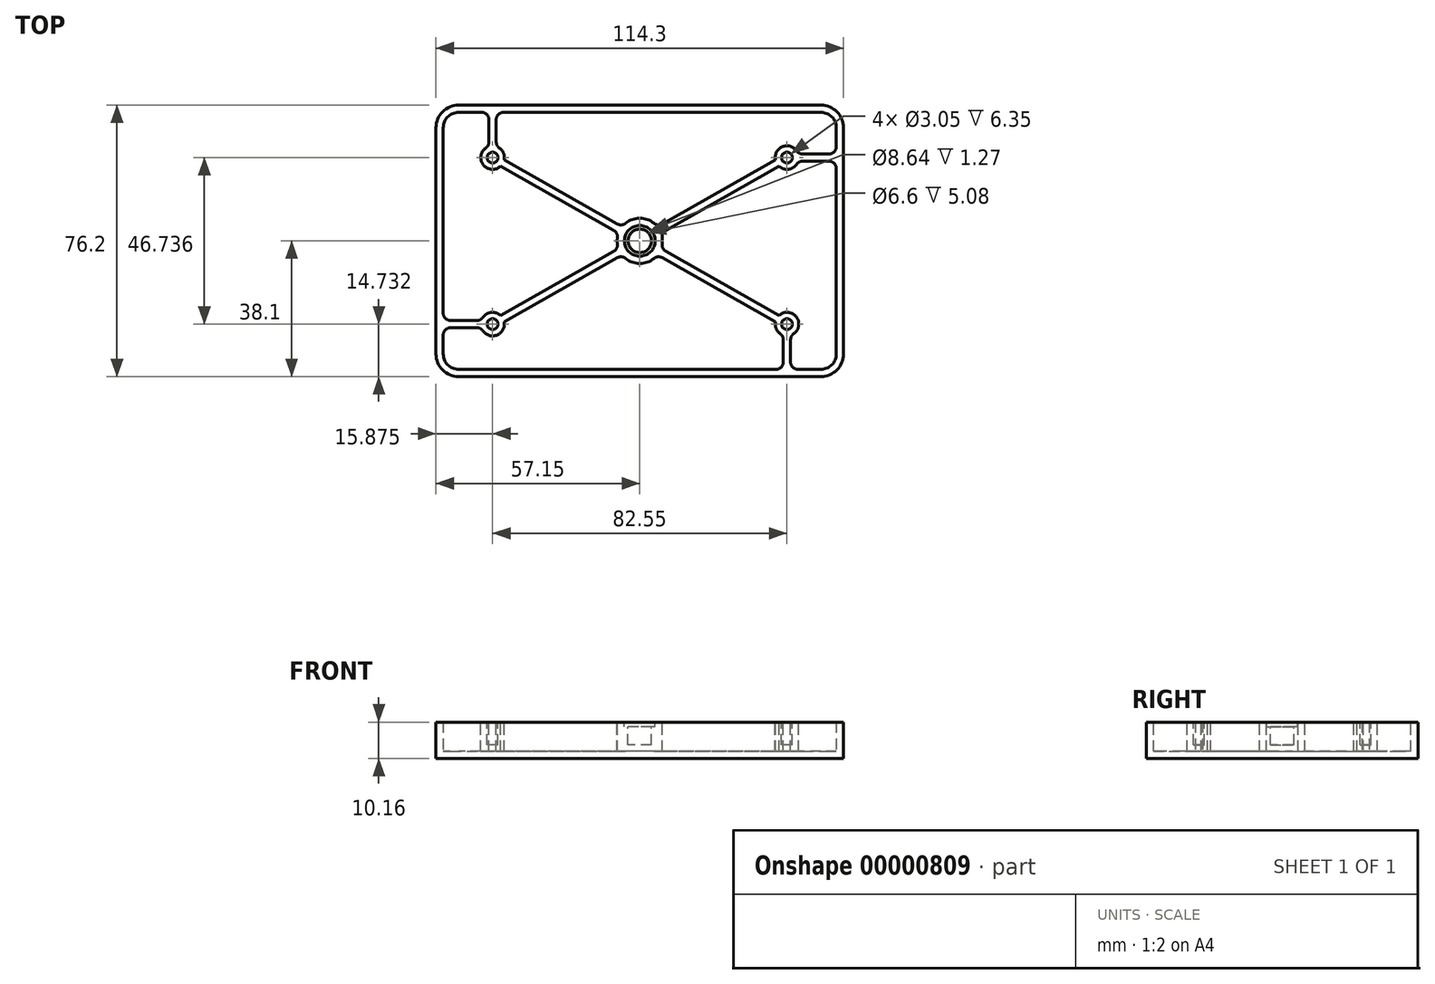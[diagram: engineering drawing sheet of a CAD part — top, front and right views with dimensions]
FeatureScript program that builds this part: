
annotation { "Feature Type Name" : "Feature", "Feature Type Description" : "" }
export const myFeature = defineFeature(function(context is Context, id is Id, definition is map)
    precondition{}
    {
        {
            var Q0;
            Q0=qCreatedBy(makeId("Top.planeOp"),FACE);
            var sketch = newSketch(context, id + "F0", { "sketchPlane" : qUnion([Q0])});
            skLineSegment(sketch, "E0.rect.bottom", {"start": v(57.15, -38.1) * mm, "end": v(-57.15, -38.1) * mm});
            skLineSegment(sketch, "E0.rect.top", {"start": v(57.15, 38.1) * mm, "end": v(-57.15, 38.1) * mm});
            skLineSegment(sketch, "E0.rect.left", {"start": v(57.15, -38.1) * mm, "end": v(57.15, 38.1) * mm});
            skLineSegment(sketch, "E0.rect.right", {"start": v(-57.15, -38.1) * mm, "end": v(-57.15, 38.1) * mm});
            skPoint(sketch, "E0.rect.middle", {"position": v(0, 0) * mm});
            skSolve(sketch);
        }
        {
            var Q0;
            Q0=makeQuery(id+"F0.imprint","IMPRINT",FACE,{"disambiguationData":[TD([[makeQuery(id+"F0.imprint","IMPRINT",EDGE,{"derivedFrom":sQuery(id+"F0.wireOp",EDGE,"E0.rect.bottom")}),-1.0]])]});
            extrude(context, id + "F1", {"entities" : qUnion([Q0]), "oppositeDirection" : true, "depth" : 10.16 * mm});
        }
        {
            var Q0;
            Q0=makeQuery(id+"F1.opExtrude","SWEPT_EDGE",EDGE,{"disambiguationData":[OSD([sQuery(id+"F0.wireOp",EDGE,"E0.rect.bottom"),sQuery(id+"F0.wireOp",EDGE,"E0.rect.right")])]});
            var Q1;
            Q1=makeQuery(id+"F1.opExtrude","SWEPT_EDGE",EDGE,{"disambiguationData":[OSD([sQuery(id+"F0.wireOp",EDGE,"E0.rect.bottom"),sQuery(id+"F0.wireOp",EDGE,"E0.rect.left")])]});
            var Q2;
            Q2=makeQuery(id+"F1.opExtrude","SWEPT_EDGE",EDGE,{"disambiguationData":[OSD([sQuery(id+"F0.wireOp",EDGE,"E0.rect.top"),sQuery(id+"F0.wireOp",EDGE,"E0.rect.left")])]});
            var Q3;
            Q3=makeQuery(id+"F1.opExtrude","SWEPT_EDGE",EDGE,{"disambiguationData":[OSD([sQuery(id+"F0.wireOp",EDGE,"E0.rect.top"),sQuery(id+"F0.wireOp",EDGE,"E0.rect.right")])]});
            fillet(context, id + "F2", {"entities" : qUnion([Q0, Q1, Q2, Q3]), "radius" : 6.35 * mm, "tangentPropagation" : true, "allowEdgeOverflow" : false});
        }
        {
            var Q0;
            Q0=makeQuery(id+"F1.opExtrude","CAP_FACE",FACE,{"disambiguationData":[OSD([sQuery(id+"F0.wireOp",EDGE,"E0.rect.bottom"),sQuery(id+"F0.wireOp",EDGE,"E0.rect.top"),sQuery(id+"F0.wireOp",EDGE,"E0.rect.left"),sQuery(id+"F0.wireOp",EDGE,"E0.rect.right")])],"isStart":true});
            shell(context, id + "F3", {"entities" : qUnion([Q0]), "thickness" : 2.03 * mm});
        }
        {
            var Q0;
            Q0=qCreatedBy(makeId("Top.planeOp"),FACE);
            var sketch = newSketch(context, id + "F4", { "sketchPlane" : qUnion([Q0])});
            skLineSegment(sketch, "E1", {"start": v(-57.15, -24.38) * mm, "end": v(-41, -24.38) * mm});
            skLineSegment(sketch, "E2", {"start": v(-41, -24.38) * mm, "end": v(41.54, 22.35) * mm});
            skLineSegment(sketch, "E3", {"start": v(41.54, 22.35) * mm, "end": v(57.15, 22.35) * mm});
            skLineSegment(sketch, "E4", {"start": v(-42.3, 38.1) * mm, "end": v(-42.3, 22.78) * mm});
            skLineSegment(sketch, "E5", {"start": v(-42.3, 22.78) * mm, "end": v(40.26, -23.96) * mm});
            skLineSegment(sketch, "E6", {"start": v(40.26, -23.96) * mm, "end": v(40.26, -38.1) * mm});
            skLineSegment(sketch, "E7.0", {"start": v(41, 24.38) * mm, "end": v(57.15, 24.38) * mm});
            skLineSegment(sketch, "E7.1", {"start": v(-41.54, -22.35) * mm, "end": v(41, 24.38) * mm});
            skLineSegment(sketch, "E7.2", {"start": v(-57.15, -22.35) * mm, "end": v(-41.54, -22.35) * mm});
            skLineSegment(sketch, "E8.0", {"start": v(42.3, -22.78) * mm, "end": v(42.3, -38.1) * mm});
            skLineSegment(sketch, "E8.1", {"start": v(-40.26, 23.96) * mm, "end": v(42.3, -22.78) * mm});
            skLineSegment(sketch, "E8.2", {"start": v(-40.26, 38.1) * mm, "end": v(-40.26, 23.96) * mm});
            skLineSegment(sketch, "E9", {"start": v(-41.54, -22.35) * mm, "end": v(-41, -24.38) * mm, "construction": true});
            skLineSegment(sketch, "E10", {"start": v(-42.3, 22.78) * mm, "end": v(-40.26, 23.96) * mm, "construction": true});
            skLineSegment(sketch, "E11", {"start": v(40.26, -23.96) * mm, "end": v(42.3, -22.78) * mm, "construction": true});
            skLineSegment(sketch, "E12", {"start": v(41, 24.38) * mm, "end": v(41.54, 22.35) * mm, "construction": true});
            skCircle(sketch, "E13", {"center": v(-41.28, -23.37) * mm, "radius": 3.3 * mm});
            skCircle(sketch, "E14", {"center": v(41.27, -23.37) * mm, "radius": 3.3 * mm});
            skCircle(sketch, "E15", {"center": v(41.27, 23.37) * mm, "radius": 3.3 * mm});
            skCircle(sketch, "E16", {"center": v(-41.28, 23.37) * mm, "radius": 3.3 * mm});
            skLineSegment(sketch, "E17", {"start": v(0, 1.17) * mm, "end": v(0, -1.17) * mm, "construction": true});
            skLineSegment(sketch, "E18", {"start": v(-57.15, -22.35) * mm, "end": v(-57.15, -24.38) * mm});
            skLineSegment(sketch, "E19", {"start": v(-40.26, 38.1) * mm, "end": v(-42.3, 38.1) * mm});
            skLineSegment(sketch, "E20", {"start": v(42.3, -38.1) * mm, "end": v(40.26, -38.1) * mm});
            skLineSegment(sketch, "E21", {"start": v(57.15, 22.35) * mm, "end": v(57.15, 24.38) * mm});
            skSolve(sketch);
        }
        {
            var Q0;
            {var subQ0=sQuery(id+"F4.wireOp",EDGE,"E18");var subQ1=sQuery(id+"F4.wireOp",EDGE,"E13");var subQ2=sQuery(id+"F4.wireOp",EDGE,"E7.2");var subQ4=sQuery(id+"F4.wireOp",EDGE,"E1");var subQ7=sQuery(id+"F4.wireOp",EDGE,"E2");var subQ8=makeQuery(id+"F4.imprint","INTERSECT",VERTEX,{"derivedFrom":[subQ7,subQ1]});var subQ9=makeQuery(id+"F4.imprint","INTERSECT",VERTEX,{"derivedFrom":[subQ4,subQ7]});var subQ11=makeQuery(id+"F4.imprint","IMPRINT",EDGE,{"disambiguationData":[TD([[subQ9,1.0]])],"derivedFrom":subQ4});var subQ13=sQuery(id+"F4.wireOp",EDGE,"E3");var subQ16=makeQuery(id+"F4.imprint","INTERSECT",VERTEX,{"derivedFrom":[subQ7,subQ13]});var subQ18=makeQuery(id+"F4.imprint","IMPRINT",EDGE,{"disambiguationData":[TD([[subQ16,1.0]])],"derivedFrom":subQ7});var subQ19=sQuery(id+"F4.wireOp",EDGE,"E21");var subQ20=sQuery(id+"F4.wireOp",EDGE,"E7.0");var subQ23=sQuery(id+"F4.wireOp",EDGE,"E19");var subQ24=sQuery(id+"F4.wireOp",EDGE,"E16");var subQ25=sQuery(id+"F4.wireOp",EDGE,"E8.2");var subQ27=sQuery(id+"F4.wireOp",EDGE,"E4");var subQ30=sQuery(id+"F4.wireOp",EDGE,"E5");var subQ31=makeQuery(id+"F4.imprint","INTERSECT",VERTEX,{"derivedFrom":[subQ30,subQ24]});var subQ32=makeQuery(id+"F4.imprint","INTERSECT",VERTEX,{"derivedFrom":[subQ27,subQ30]});var subQ34=makeQuery(id+"F4.imprint","IMPRINT",EDGE,{"disambiguationData":[TD([[subQ32,1.0]])],"derivedFrom":subQ27});var subQ36=sQuery(id+"F4.wireOp",EDGE,"E6");var subQ39=makeQuery(id+"F4.imprint","INTERSECT",VERTEX,{"derivedFrom":[subQ30,subQ36]});var subQ41=makeQuery(id+"F4.imprint","IMPRINT",EDGE,{"disambiguationData":[TD([[subQ39,1.0]])],"derivedFrom":subQ30});var subQ42=sQuery(id+"F4.wireOp",EDGE,"E20");var subQ43=sQuery(id+"F4.wireOp",EDGE,"E8.0");var subQ46=sQuery(id+"F4.wireOp",EDGE,"E7.1");var subQ48=makeQuery(id+"F4.imprint","INTERSECT",VERTEX,{"derivedFrom":[subQ20,subQ46]});var subQ50=makeQuery(id+"F4.imprint","IMPRINT",EDGE,{"disambiguationData":[TD([[subQ48,-1.0]])],"derivedFrom":subQ20});var subQ52=makeQuery(id+"F4.imprint","INTERSECT",VERTEX,{"derivedFrom":[subQ46,subQ2]});var subQ54=makeQuery(id+"F4.imprint","IMPRINT",EDGE,{"disambiguationData":[TD([[subQ52,-1.0]])],"derivedFrom":subQ46});var subQ55=sQuery(id+"F4.wireOp",EDGE,"E8.1");var subQ57=makeQuery(id+"F4.imprint","INTERSECT",VERTEX,{"derivedFrom":[subQ43,subQ55]});var subQ59=makeQuery(id+"F4.imprint","IMPRINT",EDGE,{"disambiguationData":[TD([[subQ57,-1.0]])],"derivedFrom":subQ43});var subQ61=makeQuery(id+"F4.imprint","INTERSECT",VERTEX,{"derivedFrom":[subQ55,subQ25]});var subQ63=makeQuery(id+"F4.imprint","IMPRINT",EDGE,{"disambiguationData":[TD([[subQ61,-1.0]])],"derivedFrom":subQ55});var subQ66=makeQuery(id+"F4.imprint","INTERSECT",VERTEX,{"derivedFrom":[subQ7,subQ30]});var subQ69=makeQuery(id+"F4.imprint","INTERSECT",VERTEX,{"derivedFrom":[subQ7,subQ55]});var subQ70=makeQuery(id+"F4.imprint","IMPRINT",EDGE,{"disambiguationData":[TD([[subQ66,-1.0]])],"derivedFrom":subQ7});Q0=qUnion([makeQuery(id+"F4.imprint","IMPRINT",FACE,{"disambiguationData":[TD([[makeQuery(id+"F4.imprint","IMPRINT",EDGE,{"derivedFrom":subQ0}),1.0]])]}),makeQuery(id+"F4.imprint","IMPRINT",FACE,{"disambiguationData":[TD([[subQ11,-1.0]])]}),makeQuery(id+"F4.imprint","IMPRINT",FACE,{"disambiguationData":[TD([[subQ18,-1.0]])]}),makeQuery(id+"F4.imprint","IMPRINT",FACE,{"disambiguationData":[TD([[makeQuery(id+"F4.imprint","IMPRINT",EDGE,{"derivedFrom":subQ19}),1.0]])]}),makeQuery(id+"F4.imprint","IMPRINT",FACE,{"disambiguationData":[TD([[makeQuery(id+"F4.imprint","IMPRINT",EDGE,{"derivedFrom":subQ23}),1.0]])]}),makeQuery(id+"F4.imprint","IMPRINT",FACE,{"disambiguationData":[TD([[subQ34,-1.0]])]}),makeQuery(id+"F4.imprint","IMPRINT",FACE,{"disambiguationData":[TD([[subQ41,-1.0]])]}),makeQuery(id+"F4.imprint","IMPRINT",FACE,{"disambiguationData":[TD([[makeQuery(id+"F4.imprint","IMPRINT",EDGE,{"derivedFrom":subQ42}),-1.0]])]}),makeQuery(id+"F4.imprint","IMPRINT",FACE,{"disambiguationData":[TD([[subQ50,1.0]])]}),makeQuery(id+"F4.imprint","IMPRINT",FACE,{"disambiguationData":[TD([[subQ54,1.0]])]}),makeQuery(id+"F4.imprint","IMPRINT",FACE,{"disambiguationData":[TD([[subQ59,1.0]])]}),makeQuery(id+"F4.imprint","IMPRINT",FACE,{"disambiguationData":[TD([[subQ63,1.0]])]}),makeQuery(id+"F4.imprint","IMPRINT",FACE,{"disambiguationData":[TD([[makeQuery(id+"F4.imprint","IMPRINT",EDGE,{"disambiguationData":[TD([[subQ8,-1.0]])],"derivedFrom":subQ7}),1.0]])]}),makeQuery(id+"F4.imprint","IMPRINT",FACE,{"disambiguationData":[TD([[subQ70,-1.0]])]}),makeQuery(id+"F4.imprint","IMPRINT",FACE,{"disambiguationData":[TD([[makeQuery(id+"F4.imprint","IMPRINT",EDGE,{"disambiguationData":[TD([[subQ69,-1.0]])],"derivedFrom":subQ7}),1.0]])]}),makeQuery(id+"F4.imprint","IMPRINT",FACE,{"disambiguationData":[TD([[makeQuery(id+"F4.imprint","IMPRINT",EDGE,{"disambiguationData":[TD([[subQ31,-1.0]])],"derivedFrom":subQ30}),1.0]])]}),makeQuery(id+"F4.imprint","IMPRINT",FACE,{"disambiguationData":[TD([[subQ11,1.0]])]}),makeQuery(id+"F4.imprint","IMPRINT",FACE,{"disambiguationData":[TD([[subQ70,1.0]])]}),makeQuery(id+"F4.imprint","IMPRINT",FACE,{"disambiguationData":[TD([[subQ18,1.0]])]}),makeQuery(id+"F4.imprint","IMPRINT",FACE,{"disambiguationData":[TD([[subQ34,1.0]])]}),makeQuery(id+"F4.imprint","IMPRINT",FACE,{"disambiguationData":[TD([[subQ41,1.0]])]})]);}
            var Q1;
            {var subQ0=sQuery(id+"F4.wireOp",EDGE,"E18");Q1=makeQuery(id+"F4.imprint","IMPRINT",FACE,{"disambiguationData":[TD([[makeQuery(id+"F4.imprint","IMPRINT",EDGE,{"derivedFrom":subQ0}),1.0]])]});}
            var Q2;
            {var subQ0=sQuery(id+"F4.wireOp",EDGE,"E20");Q2=makeQuery(id+"F4.imprint","IMPRINT",FACE,{"disambiguationData":[TD([[makeQuery(id+"F4.imprint","IMPRINT",EDGE,{"derivedFrom":subQ0}),-1.0]])]});}
            var Q3;
            {var subQ0=sQuery(id+"F4.wireOp",EDGE,"E21");Q3=makeQuery(id+"F4.imprint","IMPRINT",FACE,{"disambiguationData":[TD([[makeQuery(id+"F4.imprint","IMPRINT",EDGE,{"derivedFrom":subQ0}),1.0]])]});}
            var Q4;
            {var subQ0=sQuery(id+"F4.wireOp",EDGE,"E19");Q4=makeQuery(id+"F4.imprint","IMPRINT",FACE,{"disambiguationData":[TD([[makeQuery(id+"F4.imprint","IMPRINT",EDGE,{"derivedFrom":subQ0}),1.0]])]});}
            var Q5;
            Q5=makeQuery(id+"F3.opShell","OFFSET_FACE",FACE,{"disambiguationData":[OSD([sQuery(id+"F0.wireOp",EDGE,"E0.rect.bottom"),sQuery(id+"F0.wireOp",EDGE,"E0.rect.top"),sQuery(id+"F0.wireOp",EDGE,"E0.rect.left"),sQuery(id+"F0.wireOp",EDGE,"E0.rect.right")])]});
            extrude(context, id + "F5", {"entities" : qUnion([Q0, Q1, Q2, Q3, Q4]), "operationType" : NewBodyOperationType.ADD, "endBound" : BoundingType.UP_TO_BODY, "oppositeDirection" : true, "endBoundEntityBody" : qUnion([Q5]), "depth" : 25.4 * mm});
        }
        {
            var Q0;
            Q0=qCreatedBy(makeId("Top.planeOp"),FACE);
            var sketch = newSketch(context, id + "F6", { "sketchPlane" : qUnion([Q0])});
            skCircle(sketch, "E22", {"center": v(0, 0) * mm, "radius": 6.35 * mm});
            skSolve(sketch);
        }
        {
            var Q0;
            Q0=makeQuery(id+"F6.imprint","IMPRINT",FACE,{"disambiguationData":[TD([[makeQuery(id+"F6.imprint","IMPRINT",EDGE,{"derivedFrom":sQuery(id+"F6.wireOp",EDGE,"E22")}),1.0]])]});
            extrude(context, id + "F7", {"entities" : qUnion([Q0]), "operationType" : NewBodyOperationType.ADD, "endBound" : BoundingType.UP_TO_NEXT, "oppositeDirection" : true, "depth" : 25.4 * mm});
        }
        {
            var Q0;
            Q0=qCreatedBy(makeId("Top.planeOp"),FACE);
            var sketch = newSketch(context, id + "F8", { "sketchPlane" : qUnion([Q0])});
            skCircle(sketch, "E23", {"center": v(0, 0) * mm, "radius": 3.3 * mm});
            skCircle(sketch, "E24", {"center": v(41.28, 23.37) * mm, "radius": 1.52 * mm});
            skCircle(sketch, "E25", {"center": v(41.27, -23.37) * mm, "radius": 1.52 * mm});
            skCircle(sketch, "E26", {"center": v(-41.28, 23.37) * mm, "radius": 1.52 * mm});
            skCircle(sketch, "E27", {"center": v(-41.28, -23.37) * mm, "radius": 1.52 * mm});
            skSolve(sketch);
        }
        {
            var Q0;
            {Q0=qUnion([makeQuery(id+"F8.imprint","IMPRINT",FACE,{"disambiguationData":[TD([[makeQuery(id+"F8.imprint","IMPRINT",EDGE,{"derivedFrom":sQuery(id+"F8.wireOp",EDGE,"E27")}),1.0]])]}),makeQuery(id+"F8.imprint","IMPRINT",FACE,{"disambiguationData":[TD([[makeQuery(id+"F8.imprint","IMPRINT",EDGE,{"derivedFrom":sQuery(id+"F8.wireOp",EDGE,"E26")}),1.0]])]}),makeQuery(id+"F8.imprint","IMPRINT",FACE,{"disambiguationData":[TD([[makeQuery(id+"F8.imprint","IMPRINT",EDGE,{"derivedFrom":sQuery(id+"F8.wireOp",EDGE,"E25")}),1.0]])]}),makeQuery(id+"F8.imprint","IMPRINT",FACE,{"disambiguationData":[TD([[makeQuery(id+"F8.imprint","IMPRINT",EDGE,{"derivedFrom":sQuery(id+"F8.wireOp",EDGE,"E24")}),1.0]])]}),makeQuery(id+"F8.imprint","IMPRINT",FACE,{"disambiguationData":[TD([[makeQuery(id+"F8.imprint","IMPRINT",EDGE,{"derivedFrom":sQuery(id+"F8.wireOp",EDGE,"E23")}),1.0]])]})]);}
            extrude(context, id + "F9", {"entities" : qUnion([Q0]), "operationType" : NewBodyOperationType.REMOVE, "oppositeDirection" : true, "depth" : 6.35 * mm});
        }
        {
            var Q0;
            Q0=makeQuery(id+"F5.opExtrude","SWEPT_EDGE",EDGE,{"disambiguationData":[OSD([sQuery(id+"F4.wireOp",EDGE,"E1"),sQuery(id+"F4.wireOp",EDGE,"E13")])]});
            var Q1;
            Q1=makeQuery(id+"F5.opExtrude","SWEPT_EDGE",EDGE,{"disambiguationData":[OSD([sQuery(id+"F4.wireOp",EDGE,"E7.2"),sQuery(id+"F4.wireOp",EDGE,"E13")])]});
            var Q2;
            Q2=makeQuery(id+"F5.opExtrude","SWEPT_EDGE",EDGE,{"disambiguationData":[OSD([sQuery(id+"F4.wireOp",EDGE,"E7.2"),sQuery(id+"F4.wireOp",EDGE,"E13")])]});
            var Q3;
            Q3=makeQuery(id+"F5.opExtrude","SWEPT_EDGE",EDGE,{"disambiguationData":[OSD([sQuery(id+"F4.wireOp",EDGE,"E1"),sQuery(id+"F4.wireOp",EDGE,"E13")])]});
            var Q4;
            {var subQ0=sQuery(id+"F4.wireOp",EDGE,"E2");Q4=makeQuery(id+"F7.boolean.opBoolean","INTERSECT",EDGE,{"derivedFrom":[makeQuery(id+"F5.opExtrude","SWEPT_FACE",FACE,{"disambiguationData":[OSD([subQ0]),TDD([makeQuery(id+"F4.imprint","IMPRINT",EDGE,{"disambiguationData":[TD([[makeQuery(id+"F4.imprint","INTERSECT",VERTEX,{"derivedFrom":[subQ0,sQuery(id+"F4.wireOp",EDGE,"E13")]}),-1.0]])],"derivedFrom":subQ0})])]}),makeQuery(id+"F7.opExtrude","SWEPT_FACE",FACE,{"disambiguationData":[OSD([sQuery(id+"F6.wireOp",EDGE,"E22")])]})]});}
            var Q5;
            {var subQ0=sQuery(id+"F4.wireOp",EDGE,"E7.1");Q5=makeQuery(id+"F7.boolean.opBoolean","INTERSECT",EDGE,{"derivedFrom":[makeQuery(id+"F5.opExtrude","SWEPT_FACE",FACE,{"disambiguationData":[OSD([subQ0]),TDD([makeQuery(id+"F4.imprint","IMPRINT",EDGE,{"disambiguationData":[TD([[makeQuery(id+"F4.imprint","INTERSECT",VERTEX,{"derivedFrom":[sQuery(id+"F4.wireOp",EDGE,"E5"),subQ0]}),1.0]])],"derivedFrom":subQ0})])]}),makeQuery(id+"F7.opExtrude","SWEPT_FACE",FACE,{"disambiguationData":[OSD([sQuery(id+"F6.wireOp",EDGE,"E22")])]})]});}
            var Q6;
            {var subQ0=sQuery(id+"F4.wireOp",EDGE,"E5");Q6=makeQuery(id+"F7.boolean.opBoolean","INTERSECT",EDGE,{"derivedFrom":[makeQuery(id+"F5.opExtrude","SWEPT_FACE",FACE,{"disambiguationData":[OSD([subQ0]),TDD([makeQuery(id+"F4.imprint","IMPRINT",EDGE,{"disambiguationData":[TD([[makeQuery(id+"F4.imprint","INTERSECT",VERTEX,{"derivedFrom":[subQ0,sQuery(id+"F4.wireOp",EDGE,"E16")]}),-1.0]])],"derivedFrom":subQ0})])]}),makeQuery(id+"F7.opExtrude","SWEPT_FACE",FACE,{"disambiguationData":[OSD([sQuery(id+"F6.wireOp",EDGE,"E22")])]})]});}
            var Q7;
            {var subQ0=sQuery(id+"F4.wireOp",EDGE,"E8.1");Q7=makeQuery(id+"F7.boolean.opBoolean","INTERSECT",EDGE,{"derivedFrom":[makeQuery(id+"F5.opExtrude","SWEPT_FACE",FACE,{"disambiguationData":[OSD([subQ0]),TDD([makeQuery(id+"F4.imprint","IMPRINT",EDGE,{"disambiguationData":[TD([[makeQuery(id+"F4.imprint","INTERSECT",VERTEX,{"derivedFrom":[sQuery(id+"F4.wireOp",EDGE,"E7.1"),subQ0]}),1.0]])],"derivedFrom":subQ0})])]}),makeQuery(id+"F7.opExtrude","SWEPT_FACE",FACE,{"disambiguationData":[OSD([sQuery(id+"F6.wireOp",EDGE,"E22")])]})]});}
            var Q8;
            {var subQ0=sQuery(id+"F4.wireOp",EDGE,"E7.1");Q8=makeQuery(id+"F7.boolean.opBoolean","INTERSECT",EDGE,{"derivedFrom":[makeQuery(id+"F5.opExtrude","SWEPT_FACE",FACE,{"disambiguationData":[OSD([subQ0]),TDD([makeQuery(id+"F4.imprint","IMPRINT",EDGE,{"disambiguationData":[TD([[makeQuery(id+"F4.imprint","INTERSECT",VERTEX,{"derivedFrom":[subQ0,sQuery(id+"F4.wireOp",EDGE,"E8.1")]}),-1.0]])],"derivedFrom":subQ0})])]}),makeQuery(id+"F7.opExtrude","SWEPT_FACE",FACE,{"disambiguationData":[OSD([sQuery(id+"F6.wireOp",EDGE,"E22")])]})]});}
            var Q9;
            {var subQ0=sQuery(id+"F4.wireOp",EDGE,"E2");Q9=makeQuery(id+"F7.boolean.opBoolean","INTERSECT",EDGE,{"derivedFrom":[makeQuery(id+"F5.opExtrude","SWEPT_FACE",FACE,{"disambiguationData":[OSD([subQ0]),TDD([makeQuery(id+"F4.imprint","IMPRINT",EDGE,{"disambiguationData":[TD([[makeQuery(id+"F4.imprint","INTERSECT",VERTEX,{"derivedFrom":[subQ0,sQuery(id+"F4.wireOp",EDGE,"E8.1")]}),-1.0]])],"derivedFrom":subQ0})])]}),makeQuery(id+"F7.opExtrude","SWEPT_FACE",FACE,{"disambiguationData":[OSD([sQuery(id+"F6.wireOp",EDGE,"E22")])]})]});}
            var Q10;
            {var subQ0=sQuery(id+"F4.wireOp",EDGE,"E8.1");Q10=makeQuery(id+"F7.boolean.opBoolean","INTERSECT",EDGE,{"derivedFrom":[makeQuery(id+"F5.opExtrude","SWEPT_FACE",FACE,{"disambiguationData":[OSD([subQ0]),TDD([makeQuery(id+"F4.imprint","IMPRINT",EDGE,{"disambiguationData":[TD([[makeQuery(id+"F4.imprint","INTERSECT",VERTEX,{"derivedFrom":[sQuery(id+"F4.wireOp",EDGE,"E2"),subQ0]}),-1.0]])],"derivedFrom":subQ0})])]}),makeQuery(id+"F7.opExtrude","SWEPT_FACE",FACE,{"disambiguationData":[OSD([sQuery(id+"F6.wireOp",EDGE,"E22")])]})]});}
            var Q11;
            {var subQ0=sQuery(id+"F4.wireOp",EDGE,"E5");Q11=makeQuery(id+"F7.boolean.opBoolean","INTERSECT",EDGE,{"derivedFrom":[makeQuery(id+"F5.opExtrude","SWEPT_FACE",FACE,{"disambiguationData":[OSD([subQ0]),TDD([makeQuery(id+"F4.imprint","IMPRINT",EDGE,{"disambiguationData":[TD([[makeQuery(id+"F4.imprint","INTERSECT",VERTEX,{"derivedFrom":[sQuery(id+"F4.wireOp",EDGE,"E2"),subQ0]}),-1.0]])],"derivedFrom":subQ0})])]}),makeQuery(id+"F7.opExtrude","SWEPT_FACE",FACE,{"disambiguationData":[OSD([sQuery(id+"F6.wireOp",EDGE,"E22")])]})]});}
            var Q12;
            Q12=makeQuery(id+"F5.opExtrude","SWEPT_EDGE",EDGE,{"disambiguationData":[OSD([sQuery(id+"F4.wireOp",EDGE,"E3"),sQuery(id+"F4.wireOp",EDGE,"E15")])]});
            var Q13;
            Q13=makeQuery(id+"F5.opExtrude","SWEPT_EDGE",EDGE,{"disambiguationData":[OSD([sQuery(id+"F4.wireOp",EDGE,"E3"),sQuery(id+"F4.wireOp",EDGE,"E15")])]});
            var Q14;
            Q14=makeQuery(id+"F5.opExtrude","SWEPT_EDGE",EDGE,{"disambiguationData":[OSD([sQuery(id+"F4.wireOp",EDGE,"E7.0"),sQuery(id+"F4.wireOp",EDGE,"E15")])]});
            var Q15;
            Q15=makeQuery(id+"F5.opExtrude","SWEPT_EDGE",EDGE,{"disambiguationData":[OSD([sQuery(id+"F4.wireOp",EDGE,"E7.0"),sQuery(id+"F4.wireOp",EDGE,"E15")])]});
            var Q16;
            Q16=makeQuery(id+"F5.opExtrude","SWEPT_EDGE",EDGE,{"disambiguationData":[OSD([sQuery(id+"F4.wireOp",EDGE,"E8.0"),sQuery(id+"F4.wireOp",EDGE,"E14")])]});
            var Q17;
            Q17=makeQuery(id+"F5.opExtrude","SWEPT_EDGE",EDGE,{"disambiguationData":[OSD([sQuery(id+"F4.wireOp",EDGE,"E6"),sQuery(id+"F4.wireOp",EDGE,"E14")])]});
            var Q18;
            Q18=makeQuery(id+"F5.opExtrude","SWEPT_EDGE",EDGE,{"disambiguationData":[OSD([sQuery(id+"F4.wireOp",EDGE,"E8.0"),sQuery(id+"F4.wireOp",EDGE,"E14")])]});
            var Q19;
            Q19=makeQuery(id+"F5.opExtrude","SWEPT_EDGE",EDGE,{"disambiguationData":[OSD([sQuery(id+"F4.wireOp",EDGE,"E6"),sQuery(id+"F4.wireOp",EDGE,"E14")])]});
            var Q20;
            Q20=makeQuery(id+"F5.opExtrude","SWEPT_EDGE",EDGE,{"disambiguationData":[OSD([sQuery(id+"F4.wireOp",EDGE,"E8.2"),sQuery(id+"F4.wireOp",EDGE,"E16")])]});
            var Q21;
            Q21=makeQuery(id+"F5.opExtrude","SWEPT_EDGE",EDGE,{"disambiguationData":[OSD([sQuery(id+"F4.wireOp",EDGE,"E4"),sQuery(id+"F4.wireOp",EDGE,"E16")])]});
            var Q22;
            Q22=makeQuery(id+"F5.opExtrude","SWEPT_EDGE",EDGE,{"disambiguationData":[OSD([sQuery(id+"F4.wireOp",EDGE,"E8.2"),sQuery(id+"F4.wireOp",EDGE,"E16")])]});
            var Q23;
            Q23=makeQuery(id+"F5.opExtrude","SWEPT_EDGE",EDGE,{"disambiguationData":[OSD([sQuery(id+"F4.wireOp",EDGE,"E4"),sQuery(id+"F4.wireOp",EDGE,"E16")])]});
            var Q24;
            Q24=makeQuery(id+"F5.boolean.opBoolean","INTERSECT",EDGE,{"derivedFrom":[makeQuery(id+"F3.opShell","OFFSET_FACE",FACE,{"disambiguationData":[OSD([sQuery(id+"F0.wireOp",EDGE,"E0.rect.bottom")])]}),makeQuery(id+"F5.opExtrude","SWEPT_FACE",FACE,{"disambiguationData":[OSD([sQuery(id+"F4.wireOp",EDGE,"E6")])]})]});
            var Q25;
            Q25=makeQuery(id+"F5.boolean.opBoolean","INTERSECT",EDGE,{"derivedFrom":[makeQuery(id+"F3.opShell","OFFSET_FACE",FACE,{"disambiguationData":[OSD([sQuery(id+"F0.wireOp",EDGE,"E0.rect.bottom")])]}),makeQuery(id+"F5.opExtrude","SWEPT_FACE",FACE,{"disambiguationData":[OSD([sQuery(id+"F4.wireOp",EDGE,"E8.0")])]})]});
            var Q26;
            Q26=makeQuery(id+"F5.boolean.opBoolean","INTERSECT",EDGE,{"derivedFrom":[makeQuery(id+"F3.opShell","OFFSET_FACE",FACE,{"disambiguationData":[OSD([sQuery(id+"F0.wireOp",EDGE,"E0.rect.right")])]}),makeQuery(id+"F5.opExtrude","SWEPT_FACE",FACE,{"disambiguationData":[OSD([sQuery(id+"F4.wireOp",EDGE,"E7.2")])]})]});
            var Q27;
            Q27=makeQuery(id+"F5.boolean.opBoolean","INTERSECT",EDGE,{"derivedFrom":[makeQuery(id+"F3.opShell","OFFSET_FACE",FACE,{"disambiguationData":[OSD([sQuery(id+"F0.wireOp",EDGE,"E0.rect.right")])]}),makeQuery(id+"F5.opExtrude","SWEPT_FACE",FACE,{"disambiguationData":[OSD([sQuery(id+"F4.wireOp",EDGE,"E1")])]})]});
            var Q28;
            Q28=makeQuery(id+"F5.boolean.opBoolean","INTERSECT",EDGE,{"derivedFrom":[makeQuery(id+"F3.opShell","OFFSET_FACE",FACE,{"disambiguationData":[OSD([sQuery(id+"F0.wireOp",EDGE,"E0.rect.top")])]}),makeQuery(id+"F5.opExtrude","SWEPT_FACE",FACE,{"disambiguationData":[OSD([sQuery(id+"F4.wireOp",EDGE,"E8.2")])]})]});
            var Q29;
            Q29=makeQuery(id+"F5.boolean.opBoolean","INTERSECT",EDGE,{"derivedFrom":[makeQuery(id+"F3.opShell","OFFSET_FACE",FACE,{"disambiguationData":[OSD([sQuery(id+"F0.wireOp",EDGE,"E0.rect.top")])]}),makeQuery(id+"F5.opExtrude","SWEPT_FACE",FACE,{"disambiguationData":[OSD([sQuery(id+"F4.wireOp",EDGE,"E4")])]})]});
            var Q30;
            Q30=makeQuery(id+"F5.boolean.opBoolean","INTERSECT",EDGE,{"derivedFrom":[makeQuery(id+"F3.opShell","OFFSET_FACE",FACE,{"disambiguationData":[OSD([sQuery(id+"F0.wireOp",EDGE,"E0.rect.left")])]}),makeQuery(id+"F5.opExtrude","SWEPT_FACE",FACE,{"disambiguationData":[OSD([sQuery(id+"F4.wireOp",EDGE,"E7.0")])]})]});
            var Q31;
            Q31=makeQuery(id+"F5.boolean.opBoolean","INTERSECT",EDGE,{"derivedFrom":[makeQuery(id+"F3.opShell","OFFSET_FACE",FACE,{"disambiguationData":[OSD([sQuery(id+"F0.wireOp",EDGE,"E0.rect.left")])]}),makeQuery(id+"F5.opExtrude","SWEPT_FACE",FACE,{"disambiguationData":[OSD([sQuery(id+"F4.wireOp",EDGE,"E3")])]})]});
            fillet(context, id + "F10", {"entities" : qUnion([Q0, Q1, Q2, Q3, Q4, Q5, Q6, Q7, Q8, Q9, Q10, Q11, Q12, Q13, Q14, Q15, Q16, Q17, Q18, Q19, Q20, Q21, Q22, Q23, Q24, Q25, Q26, Q27, Q28, Q29, Q30, Q31]), "radius" : 2.03 * mm, "tangentPropagation" : true, "allowEdgeOverflow" : false});
        }
        {
            var Q0;
            Q0=makeQuery(id+"F7.boolean.opBoolean","MERGE",FACE,{"derivedFrom":[makeQuery(id+"F5.boolean.opBoolean","MERGE",FACE,{"derivedFrom":[makeQuery(id+"F1.opExtrude","CAP_FACE",FACE,{"disambiguationData":[OSD([sQuery(id+"F0.wireOp",EDGE,"E0.rect.bottom"),sQuery(id+"F0.wireOp",EDGE,"E0.rect.top"),sQuery(id+"F0.wireOp",EDGE,"E0.rect.left"),sQuery(id+"F0.wireOp",EDGE,"E0.rect.right")])],"isStart":true}),makeQuery(id+"F5.opExtrude","CAP_FACE",FACE,{"disambiguationData":[OSD([sQuery(id+"F4.wireOp",EDGE,"E1"),sQuery(id+"F4.wireOp",EDGE,"E2"),sQuery(id+"F4.wireOp",EDGE,"E3"),sQuery(id+"F4.wireOp",EDGE,"E4"),sQuery(id+"F4.wireOp",EDGE,"E5"),sQuery(id+"F4.wireOp",EDGE,"E6"),sQuery(id+"F4.wireOp",EDGE,"E7.0"),sQuery(id+"F4.wireOp",EDGE,"E7.1"),sQuery(id+"F4.wireOp",EDGE,"E7.2"),sQuery(id+"F4.wireOp",EDGE,"E8.0"),sQuery(id+"F4.wireOp",EDGE,"E8.1"),sQuery(id+"F4.wireOp",EDGE,"E8.2"),sQuery(id+"F4.wireOp",EDGE,"E13"),sQuery(id+"F4.wireOp",EDGE,"E14"),sQuery(id+"F4.wireOp",EDGE,"E15"),sQuery(id+"F4.wireOp",EDGE,"E16"),sQuery(id+"F4.wireOp",EDGE,"E18"),sQuery(id+"F4.wireOp",EDGE,"E19"),sQuery(id+"F4.wireOp",EDGE,"E20"),sQuery(id+"F4.wireOp",EDGE,"E21")])],"isStart":true})]}),makeQuery(id+"F7.opExtrude","CAP_FACE",FACE,{"disambiguationData":[OSD([sQuery(id+"F6.wireOp",EDGE,"E22")])],"isStart":true})]});
            var sketch = newSketch(context, id + "F11", { "sketchPlane" : qUnion([Q0])});
            skCircle(sketch, "E28", {"center": v(0, 0) * mm, "radius": 4.32 * mm});
            skSolve(sketch);
        }
        {
            var Q0;
            {var subQ0=makeQuery(id+"F11.imprint","IMPRINT",EDGE,{"derivedFrom":makeQuery(id+"F9.boolean.opBoolean","COPY",EDGE,{"derivedFrom":makeQuery(id+"F9.opExtrude","CAP_EDGE",EDGE,{"disambiguationData":[OSD([sQuery(id+"F8.wireOp",EDGE,"E23")])],"isStart":true})})});Q0=qUnion([makeQuery(id+"F11.imprint","IMPRINT",FACE,{"disambiguationData":[TD([[subQ0,1.0]])]}),makeQuery(id+"F11.imprint","IMPRINT",FACE,{"disambiguationData":[TD([[makeQuery(id+"F11.imprint","IMPRINT",EDGE,{"derivedFrom":sQuery(id+"F11.wireOp",EDGE,"E28")}),1.0]])]})]);}
            extrude(context, id + "F12", {"entities" : qUnion([Q0]), "operationType" : NewBodyOperationType.REMOVE, "oppositeDirection" : true, "depth" : 1.27 * mm});
        }
    });
